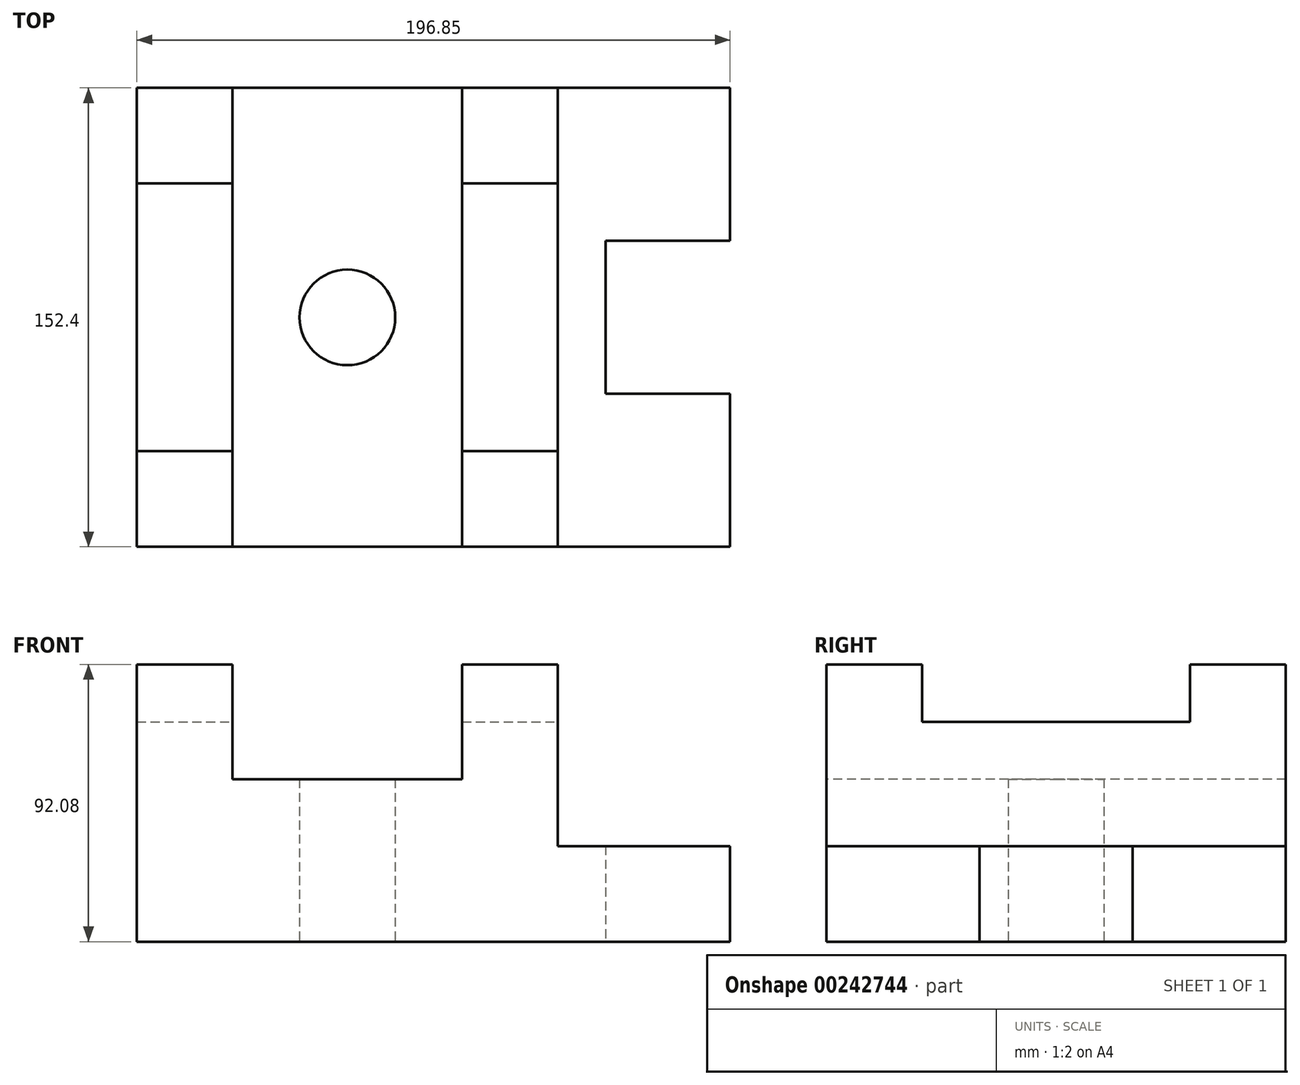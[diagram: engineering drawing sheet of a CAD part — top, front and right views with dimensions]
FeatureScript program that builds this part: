
annotation { "Feature Type Name" : "Feature", "Feature Type Description" : "" }
export const myFeature = defineFeature(function(context is Context, id is Id, definition is map)
    precondition{}
    {
        {
            var Q0;
            Q0=qCreatedBy(makeId("Top.planeOp"),FACE);
            var sketch = newSketch(context, id + "F0", { "sketchPlane" : qUnion([Q0])});
            skLineSegment(sketch, "E0.bottom", {"start": v(-127, 76.2) * mm, "end": v(-69.85, 76.2) * mm});
            skLineSegment(sketch, "E0.top", {"start": v(-127, -76.2) * mm, "end": v(127, -76.2) * mm});
            skLineSegment(sketch, "E0.left", {"start": v(-127.95, 76.96) * mm, "end": v(-127.95, 26.16) * mm});
            skLineSegment(sketch, "E0.right", {"start": v(127, 76.2) * mm, "end": v(127, 25.4) * mm});
            skPoint(sketch, "E0.middle", {"position": v(0, 0) * mm});
            skPoint(sketch, "E1", {"position": v(127, -25.4) * mm});
            skPoint(sketch, "E2", {"position": v(127, 25.4) * mm});
            skLineSegment(sketch, "E3.trimOffspring", {"start": v(127, -25.4) * mm, "end": v(127, -76.2) * mm});
            skPoint(sketch, "E4", {"position": v(-127.95, 26.16) * mm});
            skPoint(sketch, "E5", {"position": v(-127.94, -25.4) * mm});
            skLineSegment(sketch, "E6.trimOffspring", {"start": v(-127.94, -25.4) * mm, "end": v(-127, -76.2) * mm});
            skLineSegment(sketch, "E7", {"start": v(-127.95, 26.16) * mm, "end": v(-86.68, 26.16) * mm});
            skLineSegment(sketch, "E8", {"start": v(-127.94, -25.4) * mm, "end": v(-86.68, -24.64) * mm});
            skLineSegment(sketch, "E9", {"start": v(127, 25.4) * mm, "end": v(85.73, 25.4) * mm});
            skLineSegment(sketch, "E10", {"start": v(127, -25.4) * mm, "end": v(85.73, -25.4) * mm});
            skLineSegment(sketch, "E11", {"start": v(-86.68, 26.16) * mm, "end": v(-86.68, -24.64) * mm});
            skLineSegment(sketch, "E12", {"start": v(85.73, 25.4) * mm, "end": v(85.73, -25.4) * mm});
            skLineSegment(sketch, "E13", {"start": v(-69.85, 76.2) * mm, "end": v(-69.85, -76.2) * mm});
            skLineSegment(sketch, "E14", {"start": v(-38.1, 44.45) * mm, "end": v(-38.1, -44.45) * mm});
            skLineSegment(sketch, "E15", {"start": v(69.85, 76.2) * mm, "end": v(69.85, -76.2) * mm});
            skLineSegment(sketch, "E16", {"start": v(38.1, 44.45) * mm, "end": v(38.1, -44.45) * mm});
            skLineSegment(sketch, "E17", {"start": v(38.1, -44.45) * mm, "end": v(69.85, -44.45) * mm});
            skLineSegment(sketch, "E18", {"start": v(38.1, 44.45) * mm, "end": v(69.85, 44.45) * mm});
            skLineSegment(sketch, "E19", {"start": v(-69.85, 44.45) * mm, "end": v(-38.1, 44.45) * mm});
            skLineSegment(sketch, "E20", {"start": v(-69.85, -44.45) * mm, "end": v(-38.1, -44.45) * mm});
            skLineSegment(sketch, "E21.trimOffspring", {"start": v(-38.1, 76.2) * mm, "end": v(38.1, 76.2) * mm});
            skLineSegment(sketch, "E22", {"start": v(-69.85, 76.2) * mm, "end": v(-38.1, 76.2) * mm});
            skLineSegment(sketch, "E23.trimOffspring", {"start": v(69.85, 76.2) * mm, "end": v(127, 76.2) * mm});
            skLineSegment(sketch, "E24", {"start": v(38.1, 76.2) * mm, "end": v(69.85, 76.2) * mm});
            skCircle(sketch, "E25", {"center": v(0, 0) * mm, "radius": 15.88 * mm});
            skLineSegment(sketch, "E26", {"start": v(-38.1, 44.45) * mm, "end": v(-38.1, 76.2) * mm});
            skLineSegment(sketch, "E27", {"start": v(-38.1, -44.45) * mm, "end": v(-38.1, -76.2) * mm});
            skLineSegment(sketch, "E28", {"start": v(38.1, 44.45) * mm, "end": v(38.1, 76.2) * mm});
            skLineSegment(sketch, "E29", {"start": v(38.1, -44.45) * mm, "end": v(38.1, -76.2) * mm});
            skLineSegment(sketch, "E30.bottom", {"start": v(-127, 76.2) * mm, "end": v(127, 76.2) * mm});
            skLineSegment(sketch, "E30.left", {"start": v(-127.95, 76.2) * mm, "end": v(-127.95, 26.16) * mm});
            skSolve(sketch);
        }
        {
            var Q0;
            {var subQ10=sQuery(id+"F0.wireOp",EDGE,"E7");Q0=makeQuery(id+"F0.imprint","IMPRINT",FACE,{"disambiguationData":[TD([[makeQuery(id+"F0.imprint","IMPRINT",EDGE,{"derivedFrom":subQ10}),1.0]])]});}
            var Q1;
            {var subQ9=sQuery(id+"F0.wireOp",EDGE,"E9");Q1=makeQuery(id+"F0.imprint","IMPRINT",FACE,{"disambiguationData":[TD([[makeQuery(id+"F0.imprint","IMPRINT",EDGE,{"derivedFrom":subQ9}),-1.0]])]});}
            extrude(context, id + "F1", {"entities" : qUnion([Q0, Q1]), "depth" : 31.75 * mm});
        }
        {
            var Q0;
            {var subQ3=sQuery(id+"F0.wireOp",EDGE,"E19");Q0=makeQuery(id+"F0.imprint","IMPRINT",FACE,{"disambiguationData":[TD([[makeQuery(id+"F0.imprint","IMPRINT",EDGE,{"derivedFrom":subQ3}),1.0]])]});}
            var Q1;
            {var subQ3=sQuery(id+"F0.wireOp",EDGE,"E18");Q1=makeQuery(id+"F0.imprint","IMPRINT",FACE,{"disambiguationData":[TD([[makeQuery(id+"F0.imprint","IMPRINT",EDGE,{"derivedFrom":subQ3}),1.0]])]});}
            var Q2;
            {var subQ3=sQuery(id+"F0.wireOp",EDGE,"E17");Q2=makeQuery(id+"F0.imprint","IMPRINT",FACE,{"disambiguationData":[TD([[makeQuery(id+"F0.imprint","IMPRINT",EDGE,{"derivedFrom":subQ3}),-1.0]])]});}
            var Q3;
            {var subQ3=sQuery(id+"F0.wireOp",EDGE,"E20");Q3=makeQuery(id+"F0.imprint","IMPRINT",FACE,{"disambiguationData":[TD([[makeQuery(id+"F0.imprint","IMPRINT",EDGE,{"derivedFrom":subQ3}),-1.0]])]});}
            extrude(context, id + "F2", {"entities" : qUnion([Q0, Q1, Q2, Q3]), "operationType" : NewBodyOperationType.ADD, "depth" : 92.07 * mm});
        }
        {
            var Q0;
            Q0=makeQuery(id+"F0.imprint","IMPRINT",FACE,{"disambiguationData":[TD([[makeQuery(id+"F0.imprint","IMPRINT",EDGE,{"derivedFrom":sQuery(id+"F0.wireOp",EDGE,"E14")}),-1.0]])]});
            var Q1;
            Q1=makeQuery(id+"F0.imprint","IMPRINT",FACE,{"disambiguationData":[TD([[makeQuery(id+"F0.imprint","IMPRINT",EDGE,{"derivedFrom":sQuery(id+"F0.wireOp",EDGE,"E16")}),1.0]])]});
            extrude(context, id + "F3", {"entities" : qUnion([Q0, Q1]), "operationType" : NewBodyOperationType.ADD, "depth" : 73.02 * mm});
        }
        {
            var Q0;
            Q0=makeQuery(id+"F0.imprint","IMPRINT",FACE,{"disambiguationData":[TD([[makeQuery(id+"F0.imprint","IMPRINT",EDGE,{"derivedFrom":sQuery(id+"F0.wireOp",EDGE,"E14")}),1.0]])]});
            extrude(context, id + "F4", {"entities" : qUnion([Q0]), "operationType" : NewBodyOperationType.ADD, "depth" : 53.97 * mm});
        }
    });
